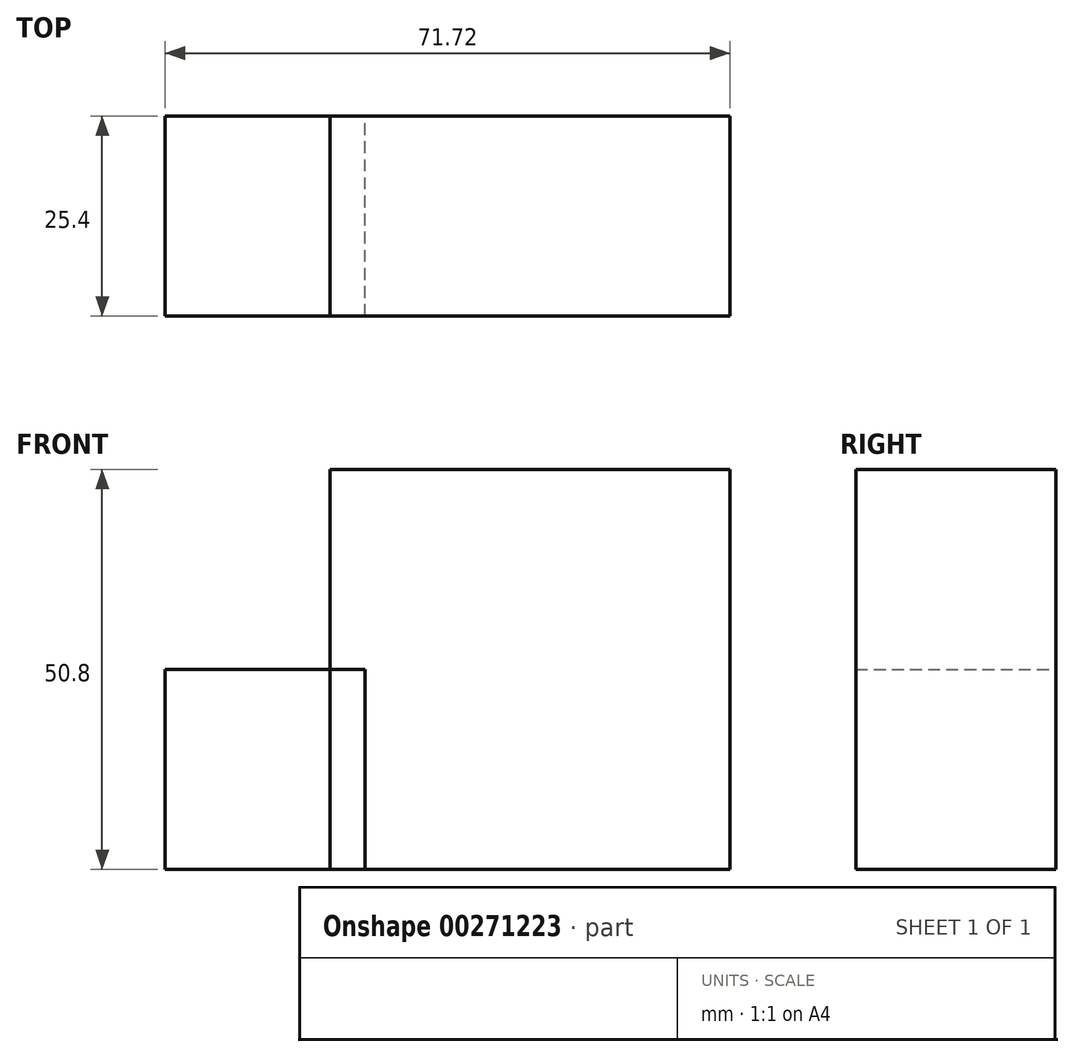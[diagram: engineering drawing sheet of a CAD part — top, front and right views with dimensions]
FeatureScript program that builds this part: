
annotation { "Feature Type Name" : "Feature", "Feature Type Description" : "" }
export const myFeature = defineFeature(function(context is Context, id is Id, definition is map)
    precondition{}
    {
        {
            var Q0;
            Q0=qCreatedBy(makeId("Front.planeOp"),FACE);
            var sketch = newSketch(context, id + "F0", { "sketchPlane" : qUnion([Q0])});
            skLineSegment(sketch, "E0.bottom", {"start": v(1.68, 0) * mm, "end": v(52.48, 0) * mm});
            skLineSegment(sketch, "E0.top", {"start": v(1.68, 50.8) * mm, "end": v(52.48, 50.8) * mm});
            skLineSegment(sketch, "E0.left", {"start": v(1.68, 0) * mm, "end": v(1.68, 50.8) * mm});
            skLineSegment(sketch, "E0.right", {"start": v(52.48, 0) * mm, "end": v(52.48, 50.8) * mm});
            skSolve(sketch);
        }
        {
            var Q0;
            Q0=qCreatedBy(makeId("Front.planeOp"),FACE);
            var sketch = newSketch(context, id + "F1", { "sketchPlane" : qUnion([Q0])});
            skLineSegment(sketch, "E1.bottom", {"start": v(6.16, 0) * mm, "end": v(-19.24, 0) * mm});
            skLineSegment(sketch, "E1.top", {"start": v(6.16, 25.4) * mm, "end": v(-19.24, 25.4) * mm});
            skLineSegment(sketch, "E1.left", {"start": v(6.16, 0) * mm, "end": v(6.16, 25.4) * mm});
            skLineSegment(sketch, "E1.right", {"start": v(-19.24, 0) * mm, "end": v(-19.24, 25.4) * mm});
            skSolve(sketch);
        }
        {
            var Q0;
            Q0=makeQuery(id+"F1.imprint","IMPRINT",FACE,{"disambiguationData":[TD([[makeQuery(id+"F1.imprint","IMPRINT",EDGE,{"derivedFrom":sQuery(id+"F1.wireOp",EDGE,"E1.bottom")}),-1.0]])]});
            var Q1;
            Q1=makeQuery(id+"F0.imprint","IMPRINT",FACE,{"disambiguationData":[TD([[makeQuery(id+"F0.imprint","IMPRINT",EDGE,{"derivedFrom":sQuery(id+"F0.wireOp",EDGE,"E0.bottom")}),1.0]])]});
            extrude(context, id + "F2", {"entities" : qUnion([Q0, Q1]), "depth" : 25.4 * mm});
        }
    });
